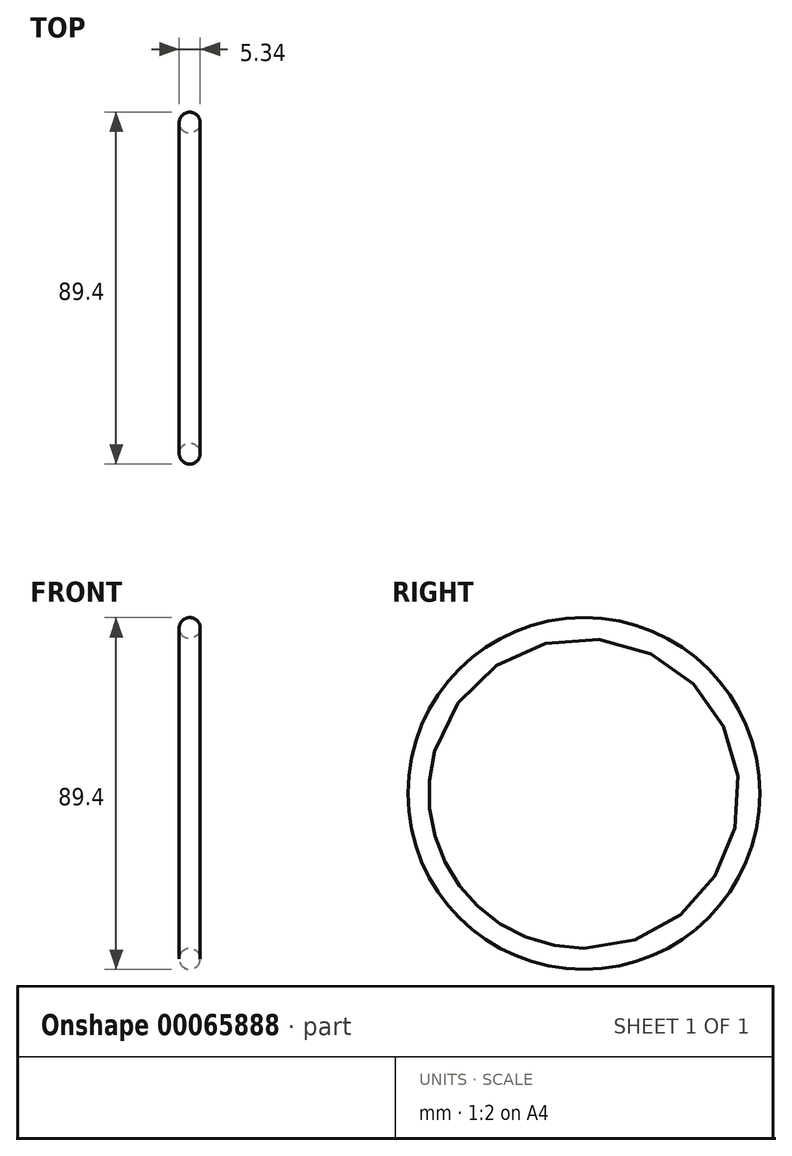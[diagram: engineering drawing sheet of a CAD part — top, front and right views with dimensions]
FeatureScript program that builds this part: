
annotation { "Feature Type Name" : "Feature", "Feature Type Description" : "" }
export const myFeature = defineFeature(function(context is Context, id is Id, definition is map)
    precondition{}
    {
        {
            var Q0;
            Q0=qCreatedBy(makeId("Front.planeOp"),FACE);
            var sketch = newSketch(context, id + "F0", { "sketchPlane" : qUnion([Q0])});
            skLineSegment(sketch, "E0", {"start": v(0, 0) * mm, "end": v(-6.06, 0) * mm, "construction": true});
            skCircle(sketch, "E1", {"center": v(0, 42.04) * mm, "radius": 2.67 * mm});
            skSolve(sketch);
        }
        {
            var Q0;
            Q0=makeQuery(id+"F0.imprint","IMPRINT",FACE,{"disambiguationData":[TD([[makeQuery(id+"F0.imprint","IMPRINT",EDGE,{"derivedFrom":sQuery(id+"F0.wireOp",EDGE,"E1")}),1.0]])]});
            var Q1;
            Q1=sQuery(id+"F0.wireOp",EDGE,"E0");
            revolve(context, id + "F1", {"entities" : qUnion([Q0]), "axis" : qUnion([Q1]), "revolveType" : RevolveType.FULL});
        }
    });
